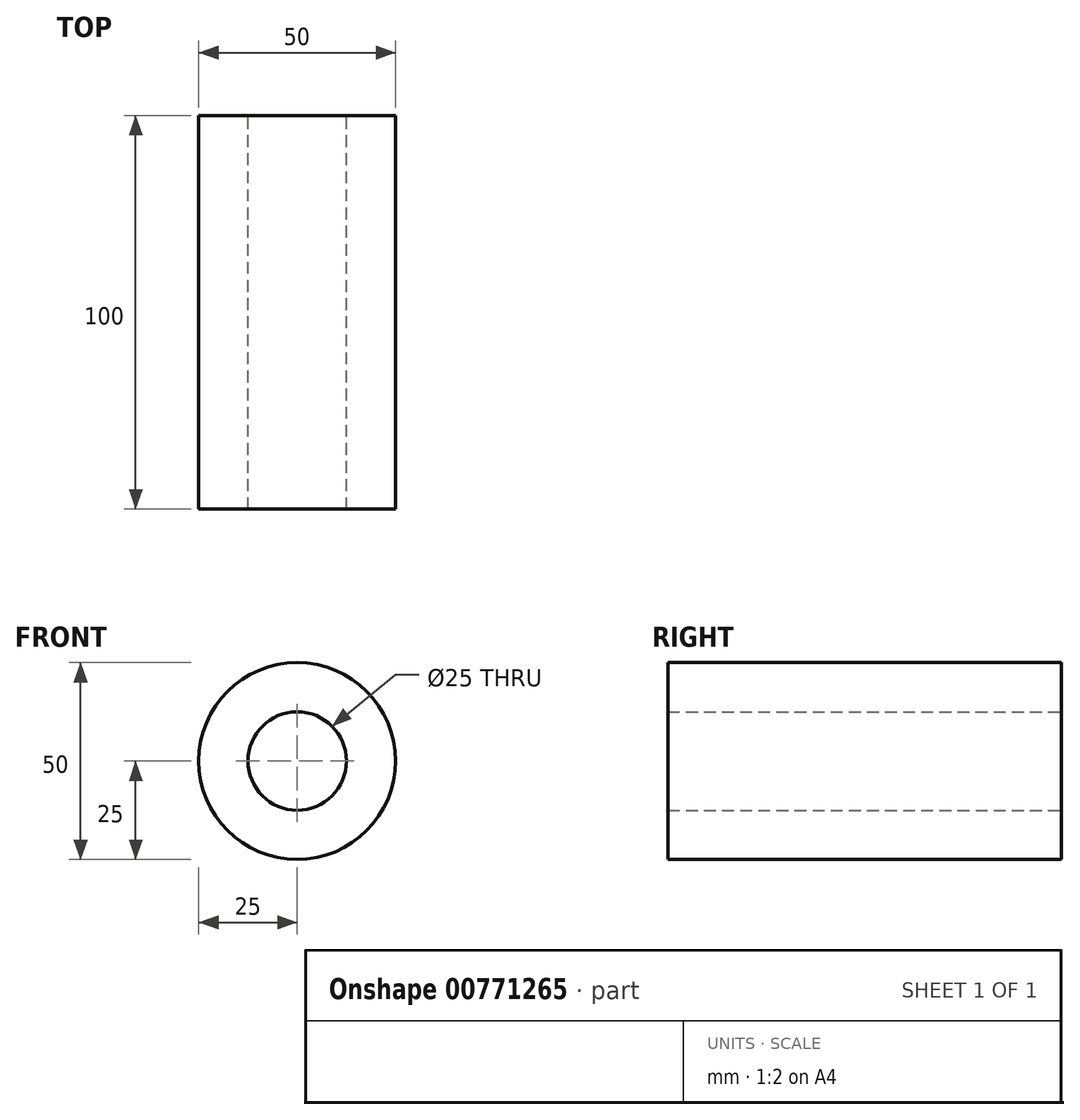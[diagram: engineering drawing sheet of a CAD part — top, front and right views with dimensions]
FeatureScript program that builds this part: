
annotation { "Feature Type Name" : "Feature", "Feature Type Description" : "" }
export const myFeature = defineFeature(function(context is Context, id is Id, definition is map)
    precondition{}
    {
        {
            var Q0;
            Q0=qCreatedBy(makeId("Front.planeOp"),FACE);
            var sketch = newSketch(context, id + "F0", { "sketchPlane" : qUnion([Q0])});
            skCircle(sketch, "E0", {"center": v(0, 0) * mm, "radius": 25 * mm});
            skCircle(sketch, "E1", {"center": v(0, 0) * mm, "radius": 12.5 * mm});
            skSolve(sketch);
        }
        {
            var Q0;
            Q0 = qSketchRegion(id + "F0", true);
            extrude(context, id + "F1", {"entities" : qUnion([Q0]), "endBound" : BoundingType.SYMMETRIC, "depth" : 100 * mm, "offsetDistance" : 25.4 * mm});
        }
    });
